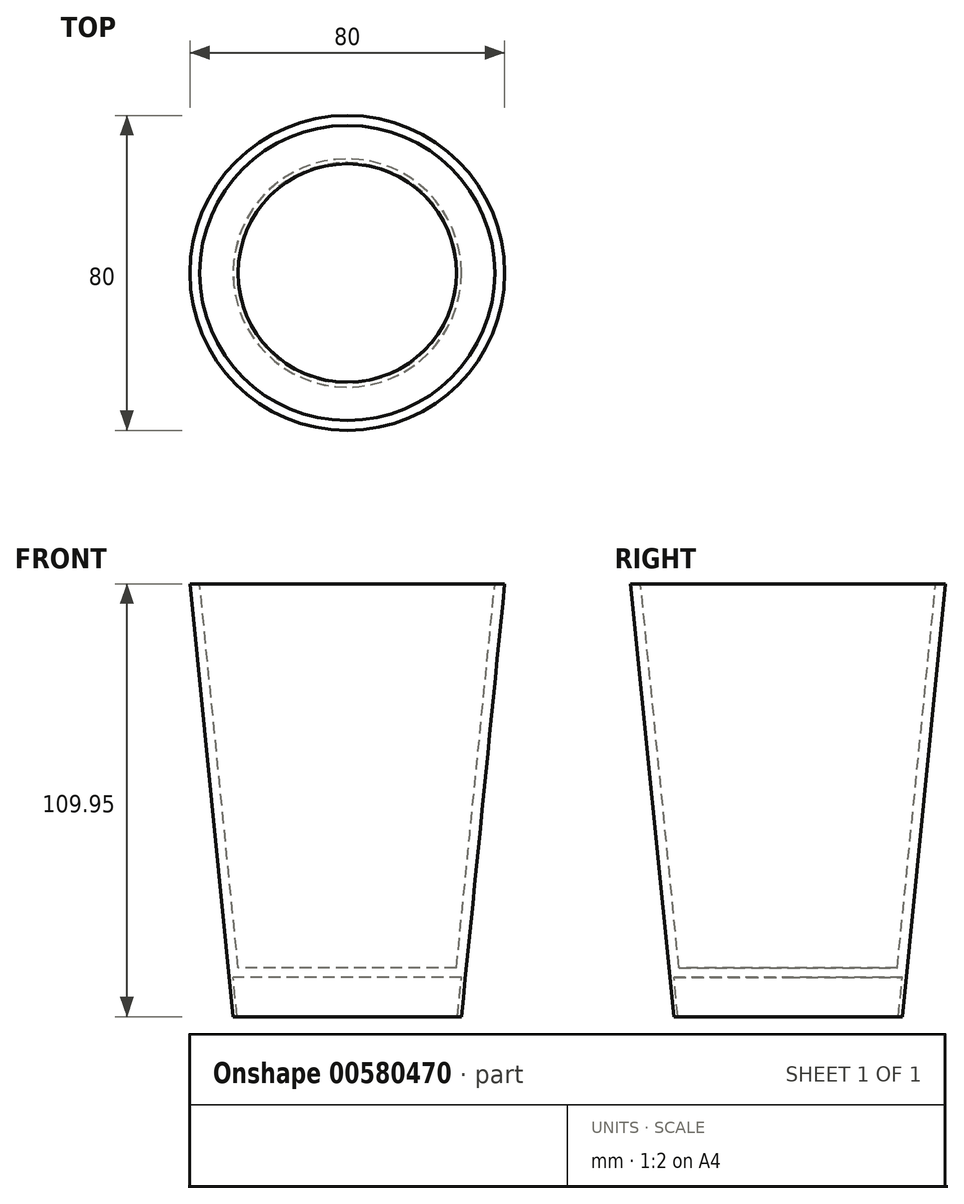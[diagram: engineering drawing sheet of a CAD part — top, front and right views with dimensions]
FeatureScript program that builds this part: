
annotation { "Feature Type Name" : "Feature", "Feature Type Description" : "" }
export const myFeature = defineFeature(function(context is Context, id is Id, definition is map)
    precondition{}
    {
        {
            var Q0;
            Q0=qCreatedBy(makeId("Front.planeOp"),FACE);
            var sketch = newSketch(context, id + "F0", { "sketchPlane" : qUnion([Q0])});
            skLineSegment(sketch, "E0", {"start": v(0, 100) * mm, "end": v(40, 100) * mm});
            skLineSegment(sketch, "E1", {"start": v(0, 0) * mm, "end": v(30, 0) * mm});
            skLineSegment(sketch, "E2", {"start": v(40, 100) * mm, "end": v(30, 0) * mm});
            skLineSegment(sketch, "E3", {"start": v(30, 0) * mm, "end": v(29, -9.95) * mm});
            skLineSegment(sketch, "E4", {"start": v(0, 100) * mm, "end": v(0, 0) * mm});
            skLineSegment(sketch, "E5", {"start": v(29, -9.95) * mm, "end": v(28, -9.85) * mm});
            skLineSegment(sketch, "E6", {"start": v(28, -9.85) * mm, "end": v(29, 0) * mm});
            skSolve(sketch);
        }
        {
            var Q0;
            Q0=makeQuery(id+"F0.imprint","IMPRINT",FACE,{"disambiguationData":[TD([[makeQuery(id+"F0.imprint","IMPRINT",EDGE,{"derivedFrom":sQuery(id+"F0.wireOp",EDGE,"E0")}),-1.0]])]});
            var Q1;
            {var subQ0=sQuery(id+"F0.wireOp",EDGE,"E3");Q1=makeQuery(id+"F0.imprint","IMPRINT",FACE,{"disambiguationData":[TD([[makeQuery(id+"F0.imprint","IMPRINT",EDGE,{"derivedFrom":subQ0}),-1.0]])]});}
            var Q2;
            Q2=sQuery(id+"F0.wireOp",EDGE,"E4");
            revolve(context, id + "F1", {"entities" : qUnion([Q0, Q1]), "axis" : qUnion([Q2]), "revolveType" : RevolveType.FULL});
        }
        {
            var Q0;
            Q0=makeQuery(id+"F1.opRevolve","SWEPT_FACE",FACE,{"disambiguationData":[OSD([sQuery(id+"F0.wireOp",EDGE,"E0")])]});
            shell(context, id + "F2", {"entities" : qUnion([Q0]), "thickness" : 2.5 * mm});
        }
    });
